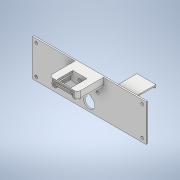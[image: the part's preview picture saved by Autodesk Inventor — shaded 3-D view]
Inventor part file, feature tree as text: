
AUTODESK INVENTOR PART (.ipt)
format: ipt  version: 2020 (Build 240168000, 168)  size: 426,496 bytes
history: native  units: mm
features: sketch x24, extrude x15, plane x6, fillet x6, loft x5, chamfer x1
ambient origin geometry x8: Origin, YZ Plane, XZ Plane, XY Plane, X Axis, Y Axis, Z Axis, Center Point
bodies: Solid1 (feature_tree), Solid2 (feature_tree)
feature tree (57):
  plane  "Work Plane34"
  plane  "Work Plane63"
  plane  "Work Plane60"
  plane  "Work Plane64"
  extrude  "Extrusion64"  Depth=6.0mm
  extrude  "Extrusion65"  Depth=12.0mm
  extrude  "Extrusion66"  Depth=15.0mm
  plane  "Work Plane65"
  sketch  "Sketch110"  dims[d641=3.0mm d642=0.0mm d643=15.0mm]
  extrude  "Extrusion67"  Depth=2.5mm
  sketch  "Sketch112"  dims[d644=40.0mm d645=2.5mm]
  extrude  "Extrusion68"  Depth=40.0mm
  extrude  "Extrusion69"  Depth=3.0mm TaperAngle=0.0deg
  sketch  "Sketch117"  dims[d655=20.0mm d656=25.0mm]
  extrude  "Extrusion72"  Depth=20.0mm
  loft  "Loft10"
  chamfer  "Chamfer5"  Distance=55.0mm
  fillet  "Fillet17"  Radius=10.0mm
  fillet  "Fillet18"  Radius=13.0mm
  fillet  "Fillet19"  Radius=10.0mm
  fillet  "Fillet20"  Radius=25.0mm
  fillet  "Fillet21"  Radius=50.0mm
  fillet  "Fillet22"  Radius=20.0mm
  sketch  "Sketch125"  dims[d674=3.2mm d675=6.5mm]
  plane  "Work Plane66"
  sketch  "Sketch127"  dims[d676=6.5mm d677=52.0mm d678=0.0mm]
  sketch  "Sketch128"  dims[d683=7.0mm d687=8.0mm]
  loft  "Loft11"
  loft  "Loft12"
  loft  "Loft13"
  loft  "Loft14"
  extrude  "Extrusion77"  Depth=20.0mm TaperAngle=0.0deg
  extrude  "Extrusion78"  Depth=12.5mm
  sketch  "Sketch133"  dims[d705=8.0mm d706=7.0mm]
  extrude  "Extrusion79"  TaperAngle=0.0deg  [1 undecoded]
  sketch  "Sketch134"  dims[d707=6.5mm d708=6.5mm]
  sketch  "Sketch135"  dims[d715=7.0mm d716=7.0mm]
  extrude  "Extrusion84"  Depth=8.0mm
  extrude  "Extrusion85"  Depth=7.0mm
  extrude  "Extrusion86"  Depth=6.5mm
  extrude  "Extrusion87"  Depth=7.0mm
  extrude  "Extrusion88"  Depth=6.0mm
  sketch  "Sketch106"  dims[d524=6.0mm d525=6.0mm]
  sketch  "Sketch107"  dims[d546=12.0mm d547=12.0mm]
  sketch  "Sketch113"  dims[d646=55.0mm d647=0.0mm d648=40.0mm]
  sketch  "Sketch114"  dims[d649=2.5mm d650=3.0mm d651=0.0mm]
  sketch  "Sketch119"  dims[d657=60.0mm d658=20.0mm d659=55.0mm d660=0.0mm d661=10.0mm d663=13.0mm d664=0.0mm d666=10.0mm d667=25.0mm d668=50.0mm d669=20.0mm]
  sketch  "Sketch120"  dims[d671=3.2mm d673=10.0mm]
  sketch  "Sketch129"  dims[d688=8.0mm d689=20.0mm d690=0.0mm]
  sketch  "Sketch130"  dims[d691=10.0mm d692=12.5mm]
  sketch  "Sketch131"  dims[d693=0.0mm d694=90.0deg d695=0.0mm d696=90.0deg]
  sketch  "Sketch132"  dims[d700=20.0mm d701=2.0mm d702=45.0deg d704=8.0mm]
  sketch  "Sketch136"  dims[d717=7.0mm d723=6.0mm]
  sketch  "Sketch137"  dims[d724=0.0mm d725=90.0deg]
  sketch  "Sketch138"  dims[d726=0.0mm d727=90.0deg]
  sketch  "Sketch139"  dims[d729=0.0mm d730=90.0deg]
  sketch  "Sketch140"  dims[d731=0.0mm d732=90.0deg d737=0.0mm d738=90.0deg d739=0.0mm d740=90.0deg d741=0.0mm d742=90.0deg d743=0.0mm d744=90.0deg d745=6.0mm d746=6.0mm d747=18.0mm d748=18.0mm d749=6.0mm d750=6.0mm d751=3.0mm d752=0.0mm d753=15.5mm d754=3.0mm d755=0.0mm d756=120.0mm d757=24.0mm d758=14.5mm d759=2.0mm d760=4.3mm d761=4.0mm d763=8.6mm d764=14.5mm d765=14.5mm d766=1.8mm d767=1.8mm d768=10.0mm d769=0.0mm d778=14.5mm d779=1.8mm d780=14.5mm d781=1.8mm d782=6.0mm d783=0.0mm d784=4.0mm d785=2.0mm d786=0.0mm d787=3.0mm d788=35.0mm d789=0.0mm d790=5.0mm d791=5.0mm d792=0.0mm d793=0.0mm d794=15.775mm d795=0.0mm d796=35.0mm d797=0.0mm d502=1.0mm d503=1.0mm d798=0.5mm d799=0.872665mm]
note: 1 required parameter value undecoded (feature->parameter linkage not recoverable at this tier; creation-order binding heuristic only, values carry confidence <= 0.55)
